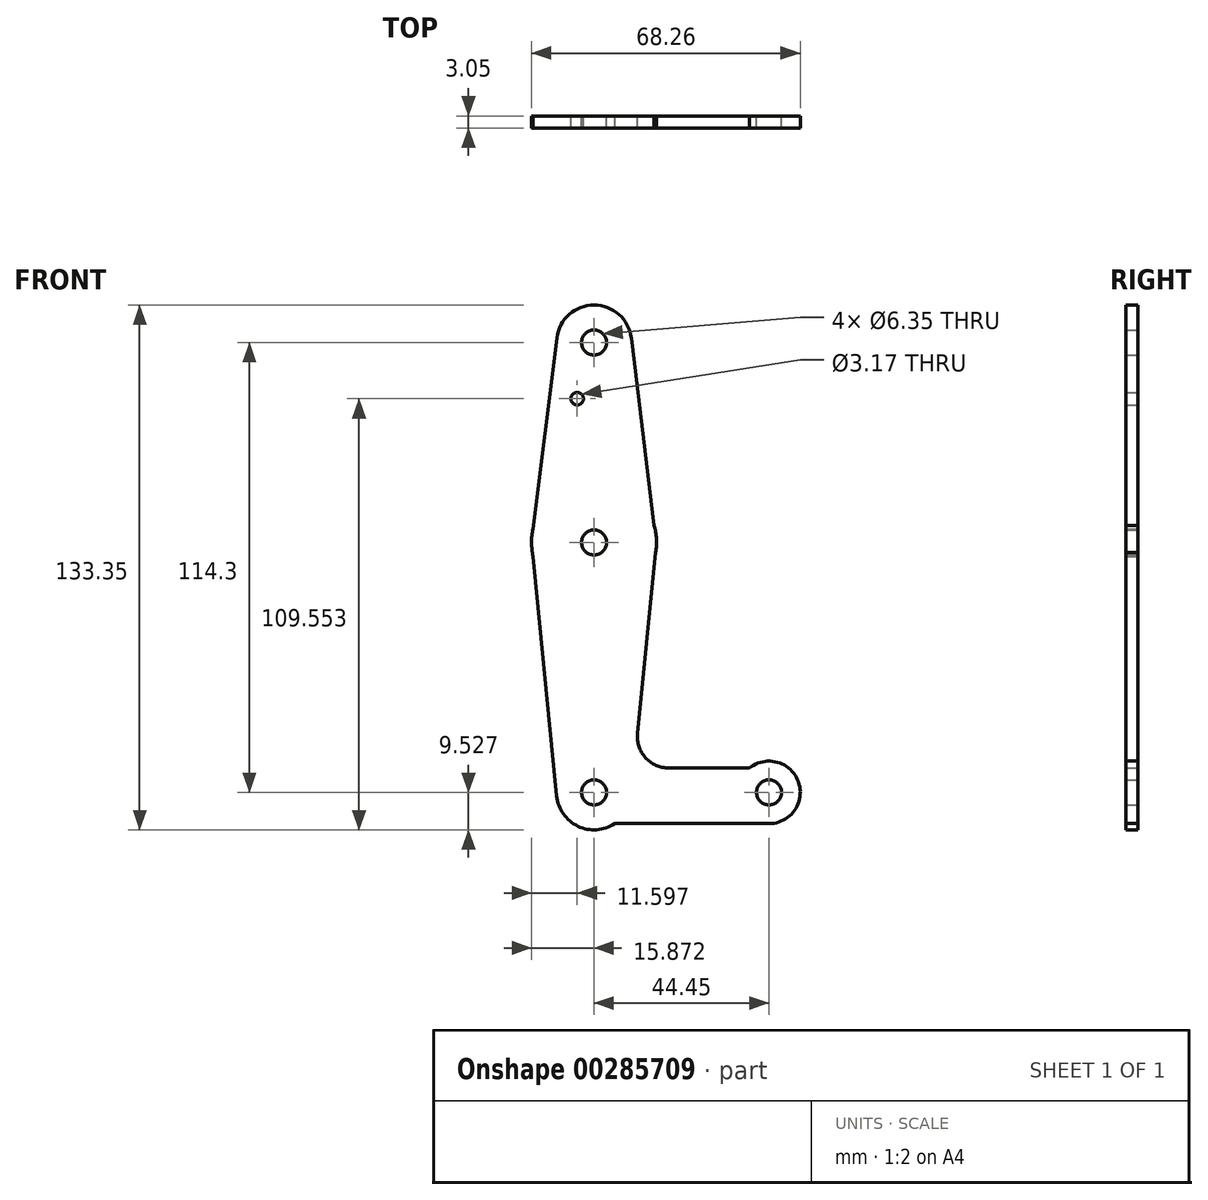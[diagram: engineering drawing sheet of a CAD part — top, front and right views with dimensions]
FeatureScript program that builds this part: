
annotation { "Feature Type Name" : "Feature", "Feature Type Description" : "" }
export const myFeature = defineFeature(function(context is Context, id is Id, definition is map)
    precondition{}
    {
        {
            var Q0;
            Q0=qCreatedBy(makeId("Front.planeOp"),FACE);
            var sketch = newSketch(context, id + "F0", { "sketchPlane" : qUnion([Q0])});
            skLineSegment(sketch, "E0", {"start": v(-39.3, 55.92) * mm, "end": v(-39.3, 5.12) * mm, "construction": true});
            skLineSegment(sketch, "E1", {"start": v(-39.3, 5.12) * mm, "end": v(-39.3, -58.38) * mm, "construction": true});
            skLineSegment(sketch, "E2", {"start": v(5.15, -58.38) * mm, "end": v(-39.3, -58.38) * mm, "construction": true});
            skCircle(sketch, "E3", {"center": v(-39.3, 55.92) * mm, "radius": 9.53 * mm});
            skCircle(sketch, "E4", {"center": v(-39.3, 5.12) * mm, "radius": 15.88 * mm});
            skCircle(sketch, "E5", {"center": v(-39.3, -58.38) * mm, "radius": 9.53 * mm});
            skCircle(sketch, "E6", {"center": v(5.15, -58.38) * mm, "radius": 7.94 * mm});
            skLineSegment(sketch, "E7", {"start": v(-55.17, 5.56) * mm, "end": v(-48.75, 57.1) * mm});
            skLineSegment(sketch, "E8", {"start": v(-48.75, 57.1) * mm, "end": v(-55.17, 5.56) * mm});
            skLineSegment(sketch, "E9", {"start": v(-55.17, 5.56) * mm, "end": v(-48.78, -59.32) * mm});
            skLineSegment(sketch, "E10", {"start": v(-23.43, 4.55) * mm, "end": v(-29.84, 57.07) * mm});
            skLineSegment(sketch, "E11", {"start": v(-29.84, 57.07) * mm, "end": v(-23.43, 4.55) * mm});
            skLineSegment(sketch, "E12", {"start": v(-23.43, 4.55) * mm, "end": v(-28.23, -43.46) * mm});
            skLineSegment(sketch, "E13", {"start": v(6.74, -52.2) * mm, "end": v(-20.32, -52.2) * mm});
            skLineSegment(sketch, "E14", {"start": v(5.15, -66.32) * mm, "end": v(-34.03, -66.32) * mm});
            skLineSegment(sketch, "E15", {"start": v(-34.03, -66.32) * mm, "end": v(5.15, -66.32) * mm, "construction": true});
            skCircle(sketch, "E16", {"center": v(-39.3, 55.92) * mm, "radius": 3.18 * mm});
            skCircle(sketch, "E17", {"center": v(-43.57, 41.64) * mm, "radius": 1.59 * mm});
            skCircle(sketch, "E18", {"center": v(-39.3, 5.12) * mm, "radius": 3.18 * mm});
            skCircle(sketch, "E19", {"center": v(-39.3, -58.38) * mm, "radius": 3.18 * mm});
            skCircle(sketch, "E20", {"center": v(5.15, -58.38) * mm, "radius": 3.18 * mm});
            skArc(sketch, "E21.filletArc", {"start": v(-28.23, -43.46) * mm, "mid": v(-26.22, -49.59) * mm, "end": v(-20.32, -52.2) * mm});
            skSolve(sketch);
        }
        {
            var Q0;
            Q0 = qSketchRegion(id + "F0", true);
            extrude(context, id + "F1", {"entities" : qUnion([Q0]), "depth" : 3.05 * mm});
        }
    });
